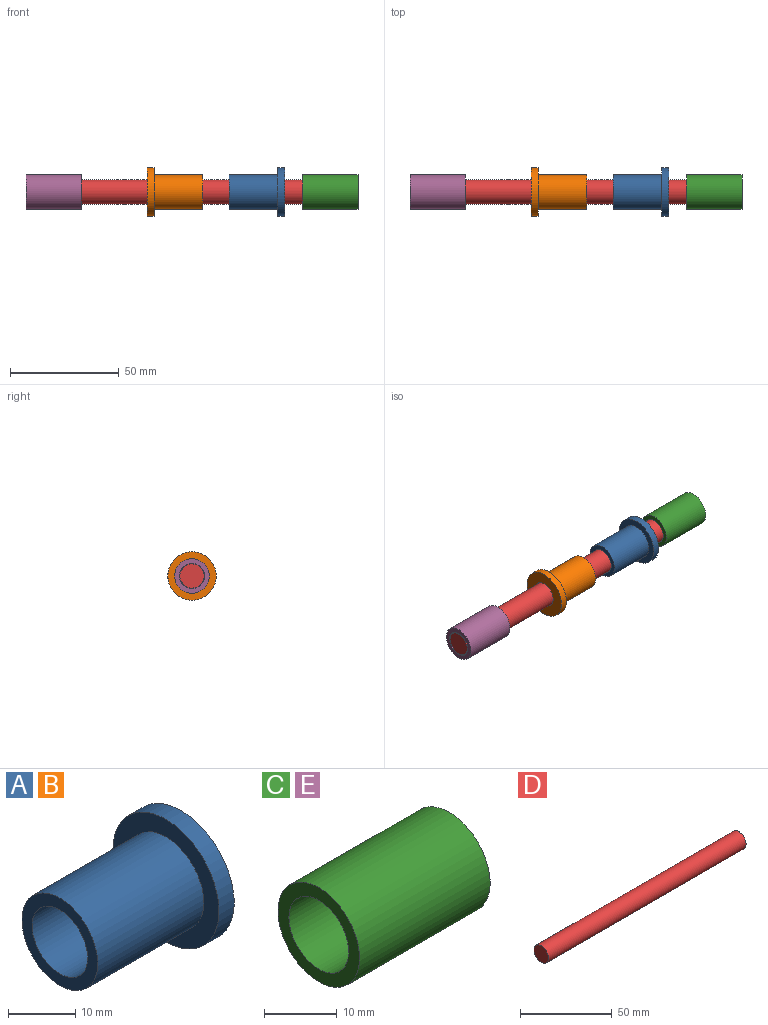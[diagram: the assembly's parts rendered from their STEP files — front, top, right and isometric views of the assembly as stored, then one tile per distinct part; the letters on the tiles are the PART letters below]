
ASSEMBLY  parts=5 mates=4
PART A: 6 faces, bbox 25.4x22.2x22.2 mm
  f0: cylinder r=7.94mm len=22.23mm, axis (-1,0,0), area 1108.4mm2, adj f3,f5
  f1: cylinder r=5.81mm len=25.4mm, axis (-1,0,0), area 927.3mm2, adj f2,f3
  f2: plane 22.23x22.23mm, normal (1,0,0), area 281.9mm2, adj f1,f4
  f3: plane 15.88x15.88mm, normal (-1,0,0), area 91.9mm2, adj f0,f1
  f4: cylinder r=11.11mm len=22.23mm, axis (1,0,0), area 221.7mm2, adj f2,f5
  f5: plane 22.23x22.23mm, normal (-1,0,0), area 190mm2, adj f0,f4
PART B: same geometry as A
PART C: 4 faces, bbox 25.4x15.9x15.9 mm
  f0: cylinder r=5.81mm len=25.4mm, axis (-1,0,0), area 927.3mm2, adj f2,f3
  f1: cylinder r=7.94mm len=25.4mm, axis (-1,0,0), area 1266.8mm2, adj f2,f3
  f2: plane 15.88x15.88mm, normal (1,0,0), area 91.9mm2, adj f0,f1
  f3: plane 15.88x15.88mm, normal (-1,0,0), area 91.9mm2, adj f0,f1
PART D: 3 faces, bbox 152.4x11.1x11.1 mm
  f0: cylinder r=5.56mm len=152.4mm, axis (-1,0,0), area 5320.4mm2, adj f1,f2
  f1: plane 11.11x11.11mm, normal (1,0,0), area 97mm2, adj f0
  f2: plane 11.11x11.11mm, normal (-1,0,0), area 97mm2, adj f0
PART E: same geometry as C
PLACE A t=(29.78,0,0)mm
PLACE B rot(axis=(0,0,1),180deg) t=(17.53,0,0)mm
PLACE C t=(63.5,30.79,-13.42)mm
PLACE D t=(12.7,0,0)mm
PLACE E t=(-63.5,30.79,-13.42)mm
MATE slider B.f0 <-> D.f0  axis (1,0,0) through (4.83,0,0)mm
MATE slider A.f0 <-> D.f0  axis (-1,0,0) through (40.89,0,0)mm
MATE slider C.f0 <-> D.f0  axis (-1,0,0) through (88.9,0,0)mm
MATE slider E.f0 <-> D.f0  axis (-1,0,0) through (-63.5,0,0)mm
